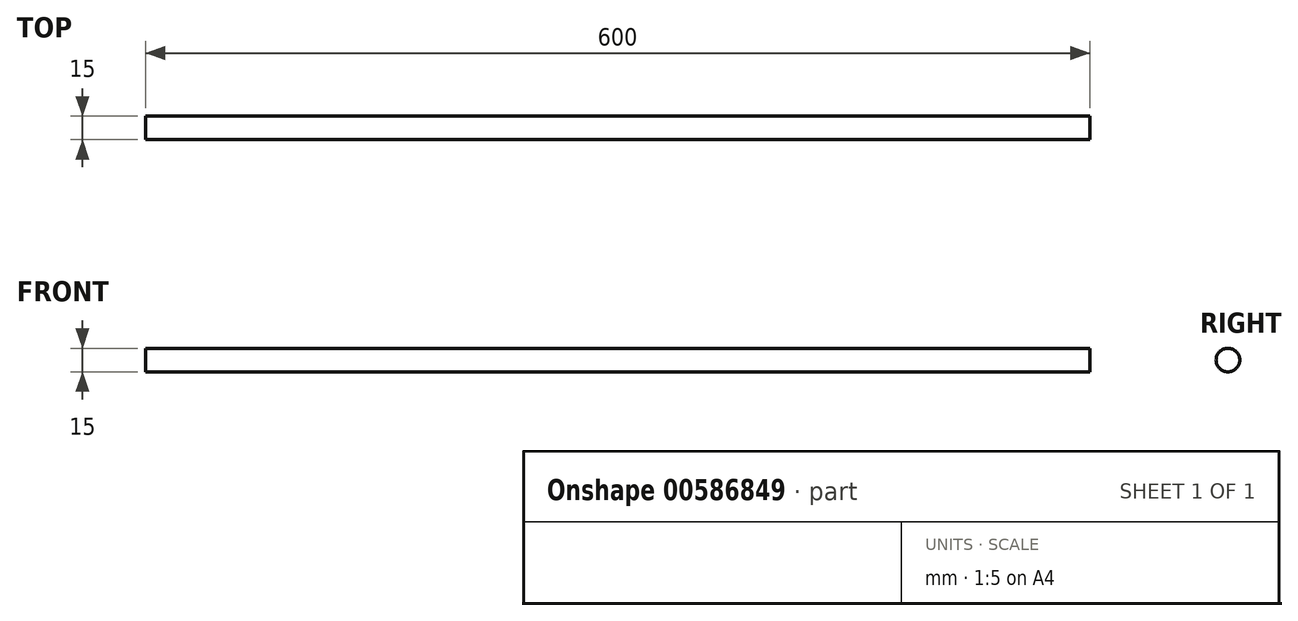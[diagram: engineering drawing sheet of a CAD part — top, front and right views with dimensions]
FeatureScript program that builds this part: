
annotation { "Feature Type Name" : "Feature", "Feature Type Description" : "" }
export const myFeature = defineFeature(function(context is Context, id is Id, definition is map)
    precondition{}
    {
        {
            var Q0;
            Q0=qCreatedBy(makeId("Right.planeOp"),FACE);
            var sketch = newSketch(context, id + "F0", { "sketchPlane" : qUnion([Q0])});
            skCircle(sketch, "E0", {"center": v(0, 0) * mm, "radius": 7.5 * mm});
            skSolve(sketch);
        }
        {
            var Q0;
            Q0=makeQuery(id+"F0.imprint","IMPRINT",FACE,{"disambiguationData":[TD([[makeQuery(id+"F0.imprint","IMPRINT",EDGE,{"derivedFrom":sQuery(id+"F0.wireOp",EDGE,"E0")}),1.0]])]});
            extrude(context, id + "F1", {"entities" : qUnion([Q0]), "depth" : 600 * mm, "offsetDistance" : 25 * mm});
        }
    });
